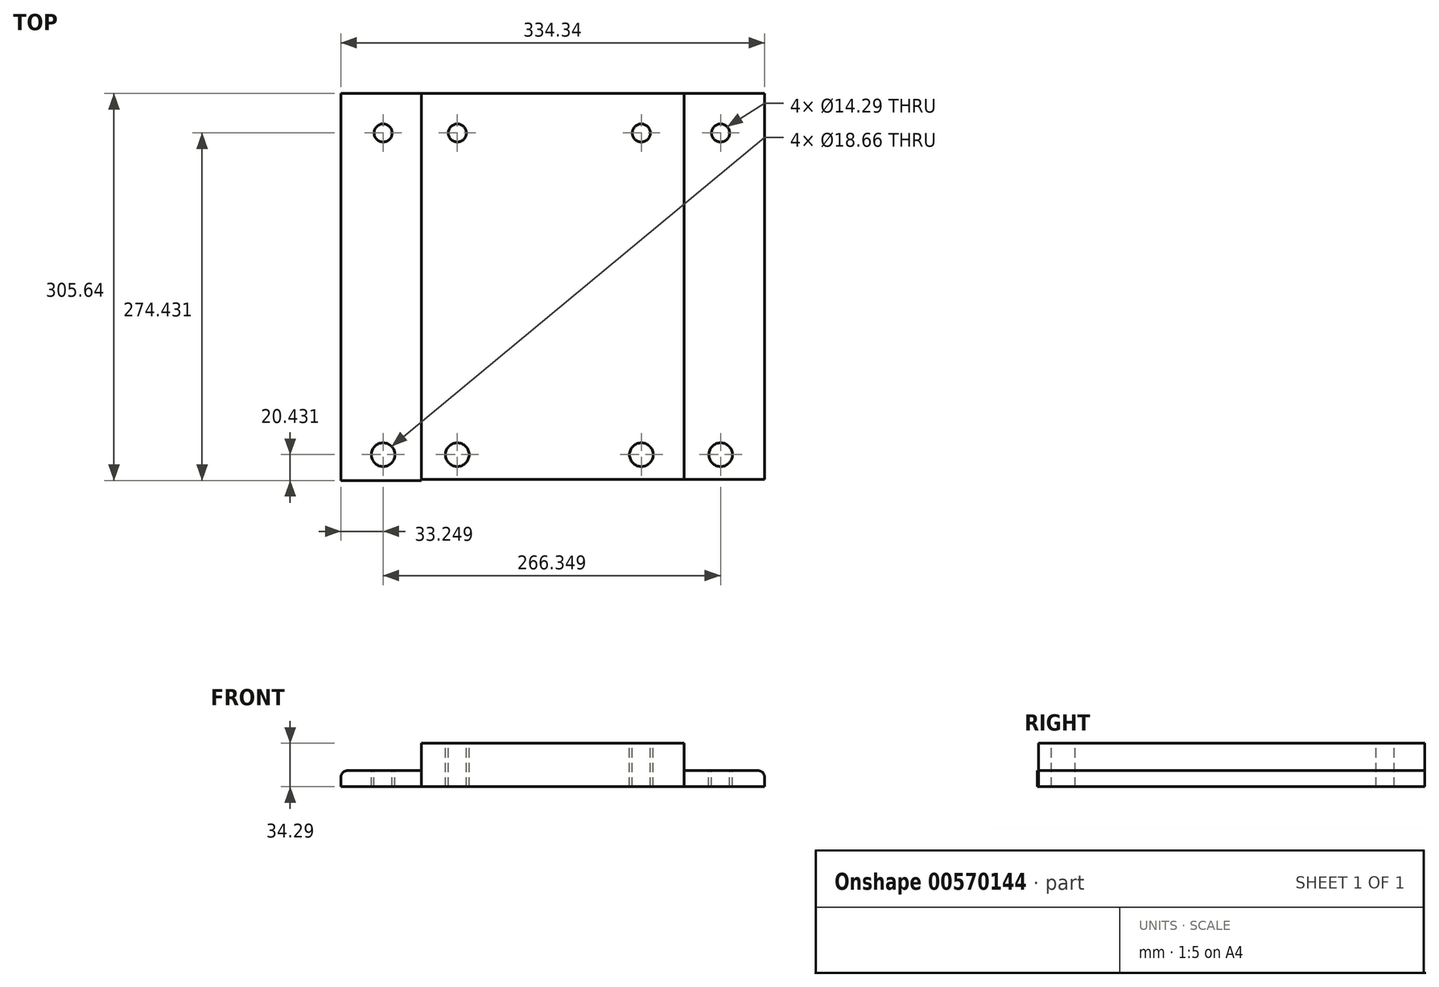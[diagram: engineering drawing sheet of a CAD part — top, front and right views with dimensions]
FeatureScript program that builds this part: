
annotation { "Feature Type Name" : "Feature", "Feature Type Description" : "" }
export const myFeature = defineFeature(function(context is Context, id is Id, definition is map)
    precondition{}
    {
        {
            var Q0;
            Q0=qCreatedBy(makeId("Top.planeOp"),FACE);
            var sketch = newSketch(context, id + "F0", { "sketchPlane" : qUnion([Q0])});
            skLineSegment(sketch, "E0.bottom", {"start": v(103.67, 152.4) * mm, "end": v(-103.67, 152.4) * mm});
            skLineSegment(sketch, "E0.top", {"start": v(103.67, -152.4) * mm, "end": v(-103.67, -152.4) * mm});
            skLineSegment(sketch, "E0.left", {"start": v(103.67, 152.4) * mm, "end": v(103.67, -152.4) * mm});
            skLineSegment(sketch, "E0.right", {"start": v(-103.67, 152.4) * mm, "end": v(-103.67, -152.4) * mm});
            skPoint(sketch, "E0.middle", {"position": v(0, 0) * mm});
            skLineSegment(sketch, "E1.bottom", {"start": v(-103.67, 152.4) * mm, "end": v(-167.17, 152.4) * mm});
            skLineSegment(sketch, "E1.top", {"start": v(-103.67, -153.24) * mm, "end": v(-167.17, -153.24) * mm});
            skLineSegment(sketch, "E1.left", {"start": v(-103.67, 152.4) * mm, "end": v(-103.67, -153.24) * mm});
            skLineSegment(sketch, "E1.right", {"start": v(-167.17, 152.4) * mm, "end": v(-167.17, -153.24) * mm});
            skLineSegment(sketch, "E2.bottom", {"start": v(103.67, 152.4) * mm, "end": v(167.17, 152.4) * mm});
            skLineSegment(sketch, "E2.top", {"start": v(103.67, -152.42) * mm, "end": v(167.17, -152.42) * mm});
            skLineSegment(sketch, "E2.left", {"start": v(103.67, 152.4) * mm, "end": v(103.67, -152.42) * mm});
            skLineSegment(sketch, "E2.right", {"start": v(167.17, 152.4) * mm, "end": v(167.17, -152.42) * mm});
            skSolve(sketch);
        }
        {
            var Q0;
            {var subQ0=sQuery(id+"F0.wireOp",EDGE,"E0.bottom");Q0=makeQuery(id+"F0.imprint","IMPRINT",FACE,{"disambiguationData":[TD([[makeQuery(id+"F0.imprint","IMPRINT",EDGE,{"derivedFrom":subQ0}),1.0]])]});}
            extrude(context, id + "F1", {"entities" : qUnion([Q0]), "depth" : 34.3 * mm, "offsetDistance" : 25.4 * mm});
        }
        {
            var Q0;
            {var subQ3=sQuery(id+"F0.wireOp",EDGE,"E1.bottom");Q0=makeQuery(id+"F0.imprint","IMPRINT",FACE,{"disambiguationData":[TD([[makeQuery(id+"F0.imprint","IMPRINT",EDGE,{"derivedFrom":subQ3}),1.0]])]});}
            var Q1;
            {var subQ3=sQuery(id+"F0.wireOp",EDGE,"E2.bottom");Q1=makeQuery(id+"F0.imprint","IMPRINT",FACE,{"disambiguationData":[TD([[makeQuery(id+"F0.imprint","IMPRINT",EDGE,{"derivedFrom":subQ3}),-1.0]])]});}
            extrude(context, id + "F2", {"entities" : qUnion([Q0, Q1]), "operationType" : NewBodyOperationType.ADD, "depth" : 12.7 * mm, "offsetDistance" : 25.4 * mm});
        }
        {
            var Q0;
            Q0=makeQuery(id+"F2.opExtrude","CAP_EDGE",EDGE,{"disambiguationData":[OSD([sQuery(id+"F0.wireOp",EDGE,"E1.right")])],"isStart":false});
            var Q1;
            Q1=makeQuery(id+"F1.opExtrude","CAP_EDGE",EDGE,{"disambiguationData":[OSD([sQuery(id+"F0.wireOp",EDGE,"E1.left")])],"isStart":false});
            var Q2;
            Q2=makeQuery(id+"F1.opExtrude","CAP_EDGE",EDGE,{"disambiguationData":[OSD([sQuery(id+"F0.wireOp",EDGE,"E2.left")])],"isStart":false});
            var Q3;
            Q3=makeQuery(id+"F2.opExtrude","CAP_EDGE",EDGE,{"disambiguationData":[OSD([sQuery(id+"F0.wireOp",EDGE,"E2.right")])],"isStart":false});
            fillet(context, id + "F3", {"entities" : qUnion([Q0, Q1, Q2, Q3]), "radius" : 5.08 * mm, "tangentPropagation" : true, "allowEdgeOverflow" : false});
        }
        {
            var Q0;
            Q0=makeQuery(id+"F1.opExtrude","CAP_FACE",FACE,{"disambiguationData":[OSD([sQuery(id+"F0.wireOp",EDGE,"E0.bottom"),sQuery(id+"F0.wireOp",EDGE,"E0.top"),sQuery(id+"F0.wireOp",EDGE,"E1.left"),sQuery(id+"F0.wireOp",EDGE,"E2.left")])],"isStart":false});
            var sketch = newSketch(context, id + "F4", { "sketchPlane" : qUnion([Q0])});
            skCircle(sketch, "E3", {"center": v(-133.92, 121.2) * mm, "radius": 7.14 * mm});
            skCircle(sketch, "E4", {"center": v(-75.38, 121.2) * mm, "radius": 7.14 * mm});
            skCircle(sketch, "E5", {"center": v(69.86, 121.2) * mm, "radius": 7.14 * mm});
            skCircle(sketch, "E6", {"center": v(132.43, 121.2) * mm, "radius": 7.14 * mm});
            skCircle(sketch, "E7", {"center": v(-133.92, -132.8) * mm, "radius": 9.33 * mm});
            skCircle(sketch, "E8", {"center": v(-75.38, -132.8) * mm, "radius": 9.33 * mm});
            skCircle(sketch, "E9", {"center": v(69.86, -132.8) * mm, "radius": 9.33 * mm});
            skCircle(sketch, "E10", {"center": v(132.43, -132.8) * mm, "radius": 9.33 * mm});
            skSolve(sketch);
        }
        {
            var Q0;
            Q0=makeQuery(id+"F4.imprint","IMPRINT",FACE,{"disambiguationData":[TD([[makeQuery(id+"F4.imprint","IMPRINT",EDGE,{"derivedFrom":sQuery(id+"F4.wireOp",EDGE,"E3")}),1.0]])]});
            var Q1;
            Q1=makeQuery(id+"F4.imprint","IMPRINT",FACE,{"disambiguationData":[TD([[makeQuery(id+"F4.imprint","IMPRINT",EDGE,{"derivedFrom":sQuery(id+"F4.wireOp",EDGE,"E4")}),1.0]])]});
            var Q2;
            Q2=makeQuery(id+"F4.imprint","IMPRINT",FACE,{"disambiguationData":[TD([[makeQuery(id+"F4.imprint","IMPRINT",EDGE,{"derivedFrom":sQuery(id+"F4.wireOp",EDGE,"E5")}),1.0]])]});
            var Q3;
            Q3=makeQuery(id+"F4.imprint","IMPRINT",FACE,{"disambiguationData":[TD([[makeQuery(id+"F4.imprint","IMPRINT",EDGE,{"derivedFrom":sQuery(id+"F4.wireOp",EDGE,"E6")}),1.0]])]});
            var Q4;
            Q4=makeQuery(id+"F4.imprint","IMPRINT",FACE,{"disambiguationData":[TD([[makeQuery(id+"F4.imprint","IMPRINT",EDGE,{"derivedFrom":sQuery(id+"F4.wireOp",EDGE,"E10")}),1.0]])]});
            var Q5;
            Q5=makeQuery(id+"F4.imprint","IMPRINT",FACE,{"disambiguationData":[TD([[makeQuery(id+"F4.imprint","IMPRINT",EDGE,{"derivedFrom":sQuery(id+"F4.wireOp",EDGE,"E9")}),1.0]])]});
            var Q6;
            Q6=makeQuery(id+"F4.imprint","IMPRINT",FACE,{"disambiguationData":[TD([[makeQuery(id+"F4.imprint","IMPRINT",EDGE,{"derivedFrom":sQuery(id+"F4.wireOp",EDGE,"E8")}),1.0]])]});
            var Q7;
            Q7=makeQuery(id+"F4.imprint","IMPRINT",FACE,{"disambiguationData":[TD([[makeQuery(id+"F4.imprint","IMPRINT",EDGE,{"derivedFrom":sQuery(id+"F4.wireOp",EDGE,"E7")}),1.0]])]});
            extrude(context, id + "F5", {"entities" : qUnion([Q0, Q1, Q2, Q3, Q4, Q5, Q6, Q7]), "operationType" : NewBodyOperationType.REMOVE, "endBound" : BoundingType.THROUGH_ALL, "oppositeDirection" : true, "depth" : 25.4 * mm, "offsetDistance" : 25.4 * mm});
        }
    });
